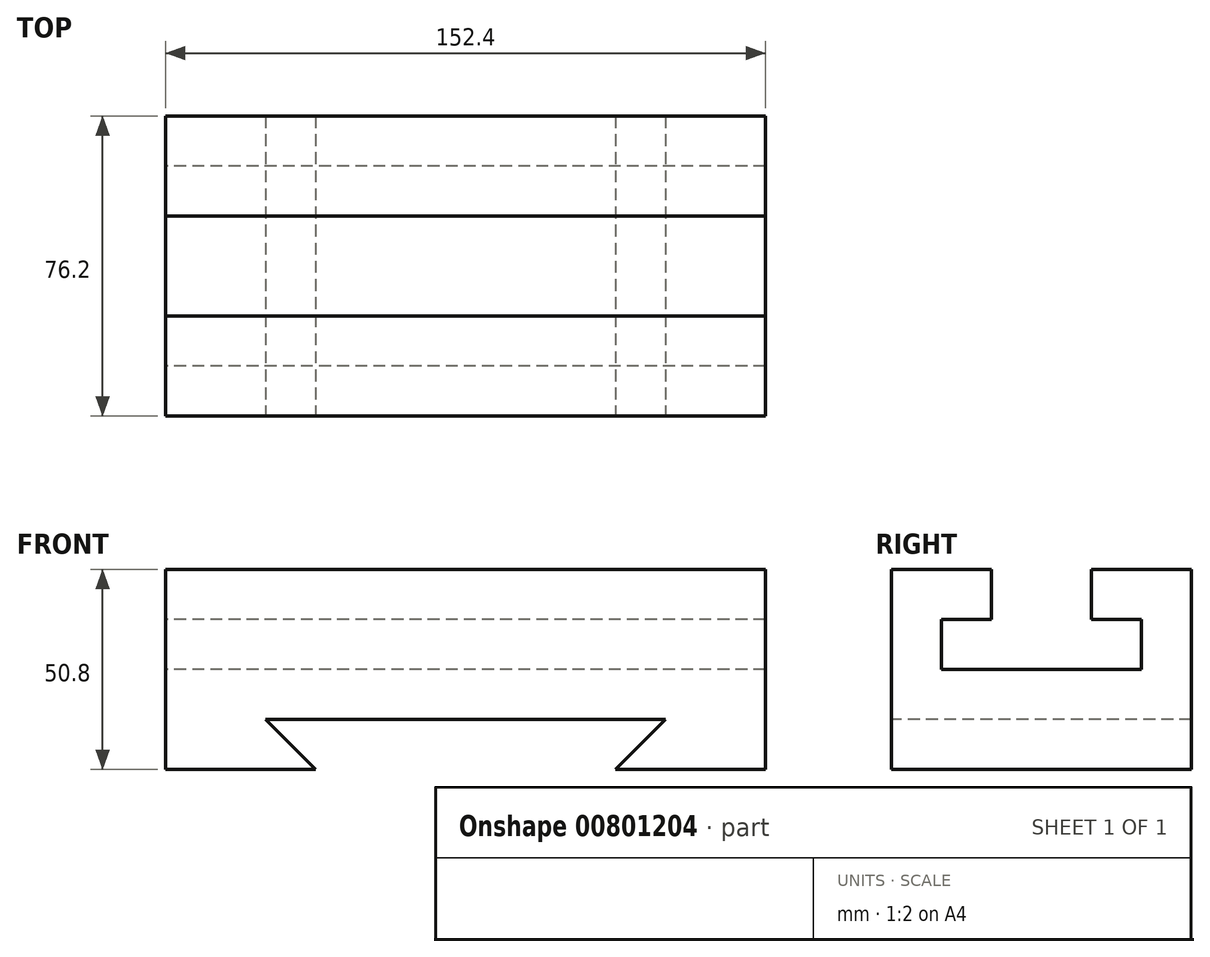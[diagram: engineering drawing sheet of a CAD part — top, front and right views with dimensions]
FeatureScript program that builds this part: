
annotation { "Feature Type Name" : "Feature", "Feature Type Description" : "" }
export const myFeature = defineFeature(function(context is Context, id is Id, definition is map)
    precondition{}
    {
        {
            var Q0;
            Q0=qCreatedBy(makeId("Right.planeOp"),FACE);
            var sketch = newSketch(context, id + "F0", { "sketchPlane" : qUnion([Q0])});
            skLineSegment(sketch, "E0", {"start": v(-32.1, -15.1) * mm, "end": v(44.1, -15.1) * mm});
            skLineSegment(sketch, "E1", {"start": v(-32.1, 35.7) * mm, "end": v(-32.1, -15.1) * mm});
            skLineSegment(sketch, "E2", {"start": v(44.1, 35.7) * mm, "end": v(44.1, -15.1) * mm});
            skLineSegment(sketch, "E3", {"start": v(-32.1, 35.7) * mm, "end": v(-6.7, 35.7) * mm});
            skLineSegment(sketch, "E4", {"start": v(44.1, 35.7) * mm, "end": v(18.7, 35.7) * mm});
            skLineSegment(sketch, "E5", {"start": v(-6.7, 35.7) * mm, "end": v(-6.7, 23) * mm});
            skLineSegment(sketch, "E6", {"start": v(18.7, 35.7) * mm, "end": v(18.7, 23) * mm});
            skLineSegment(sketch, "E7", {"start": v(-6.7, 23) * mm, "end": v(-19.4, 23) * mm});
            skLineSegment(sketch, "E8", {"start": v(18.7, 23) * mm, "end": v(31.4, 23) * mm});
            skLineSegment(sketch, "E9", {"start": v(-19.4, 23) * mm, "end": v(-19.4, 10.3) * mm});
            skLineSegment(sketch, "E10", {"start": v(31.4, 23) * mm, "end": v(31.4, 10.3) * mm});
            skLineSegment(sketch, "E11", {"start": v(-19.4, 10.3) * mm, "end": v(31.4, 10.3) * mm});
            skSolve(sketch);
        }
        {
            var Q0;
            Q0=makeQuery(id+"F0.imprint","IMPRINT",FACE,{"disambiguationData":[TD([[makeQuery(id+"F0.imprint","IMPRINT",EDGE,{"derivedFrom":sQuery(id+"F0.wireOp",EDGE,"E0")}),1.0]])]});
            extrude(context, id + "F1", {"entities" : qUnion([Q0]), "depth" : 152.4 * mm, "offsetDistance" : 25.4 * mm});
        }
        {
            var Q0;
            Q0=makeQuery(id+"F1.opExtrude","SWEPT_FACE",FACE,{"disambiguationData":[OSD([sQuery(id+"F0.wireOp",EDGE,"E1")])]});
            var sketch = newSketch(context, id + "F2", { "sketchPlane" : qUnion([Q0])});
            skLineSegment(sketch, "E12", {"start": v(38.1, -15.1) * mm, "end": v(25.4, -2.4) * mm});
            skLineSegment(sketch, "E13", {"start": v(114.3, -15.1) * mm, "end": v(127, -2.4) * mm});
            skLineSegment(sketch, "E14", {"start": v(25.4, -2.4) * mm, "end": v(127, -2.4) * mm});
            skSolve(sketch);
        }
        {
            var Q0;
            {var subQ0=sQuery(id+"F2.wireOp",EDGE,"E12");Q0=makeQuery(id+"F2.imprint","IMPRINT",FACE,{"disambiguationData":[TD([[makeQuery(id+"F2.imprint","IMPRINT",EDGE,{"derivedFrom":subQ0}),-1.0]])]});}
            extrude(context, id + "F3", {"entities" : qUnion([Q0]), "operationType" : NewBodyOperationType.REMOVE, "oppositeDirection" : true, "depth" : 76.2 * mm, "offsetDistance" : 25.4 * mm});
        }
    });
